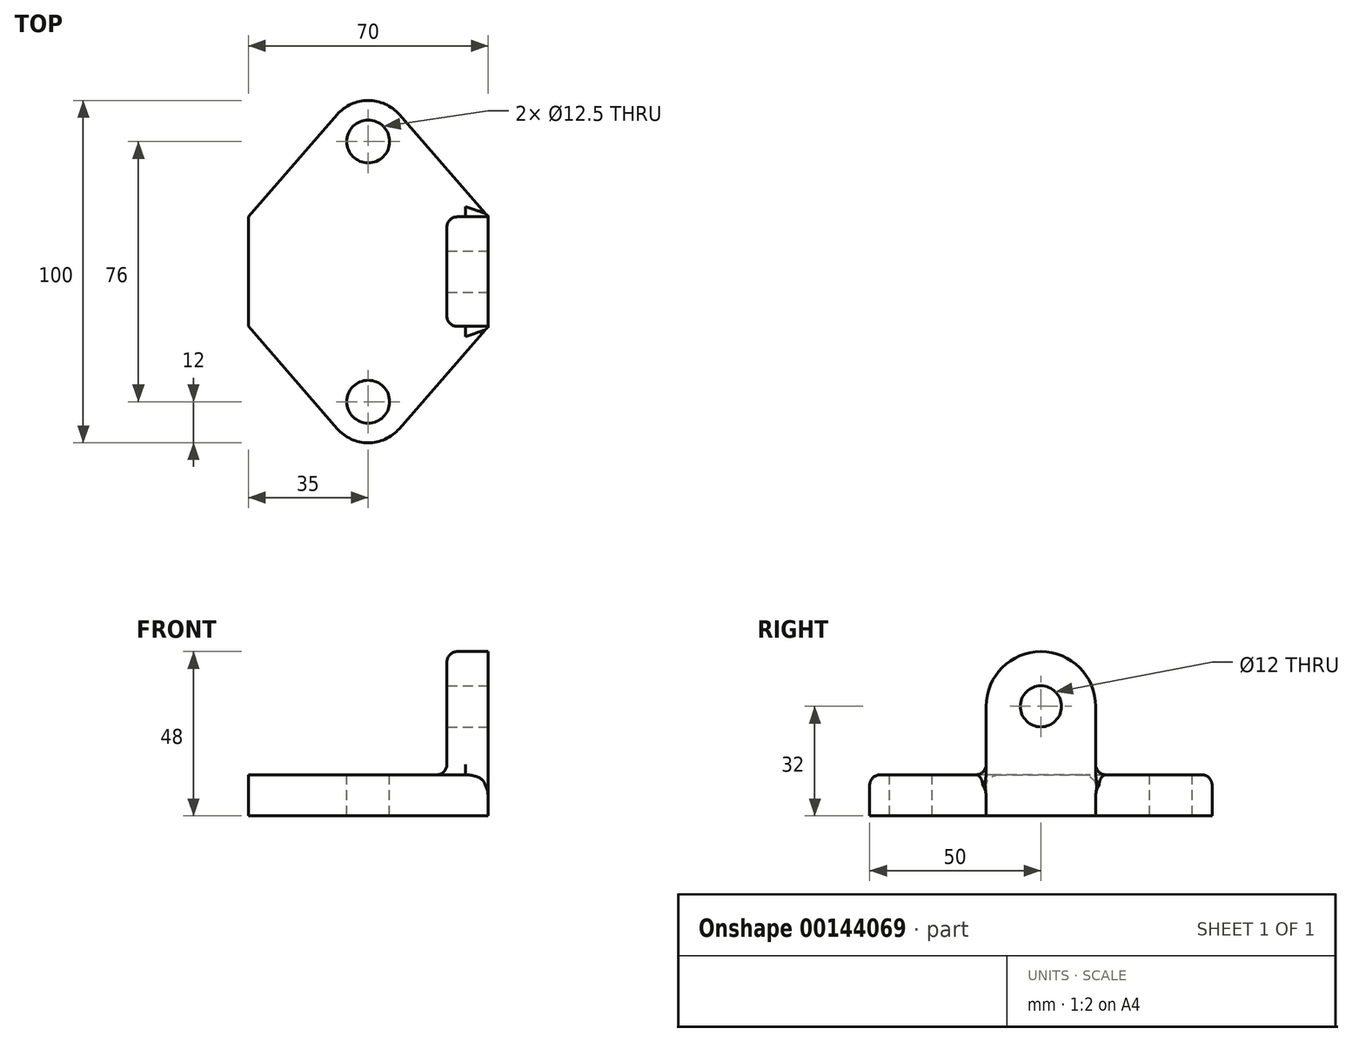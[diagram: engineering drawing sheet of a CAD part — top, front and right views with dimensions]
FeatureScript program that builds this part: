
annotation { "Feature Type Name" : "Feature", "Feature Type Description" : "" }
export const myFeature = defineFeature(function(context is Context, id is Id, definition is map)
    precondition{}
    {
        {
            var Q0;
            Q0=qCreatedBy(makeId("Top.planeOp"),FACE);
            var sketch = newSketch(context, id + "F0", { "sketchPlane" : qUnion([Q0])});
            skLineSegment(sketch, "E0", {"start": v(0, 62.74) * mm, "end": v(0, -56.64) * mm, "construction": true});
            skLineSegment(sketch, "E1.bottom", {"start": v(-35, 0) * mm, "end": v(35, 0) * mm});
            skLineSegment(sketch, "E1.left", {"start": v(-35, 0) * mm, "end": v(-35, -16) * mm});
            skLineSegment(sketch, "E1.right", {"start": v(35, 0) * mm, "end": v(35, -16) * mm});
            skLineSegment(sketch, "E2", {"start": v(-35, -16) * mm, "end": v(-9.06, -45.87) * mm});
            skLineSegment(sketch, "E3", {"start": v(-9.06, -45.87) * mm, "end": v(9.06, -45.87) * mm});
            skLineSegment(sketch, "E4", {"start": v(9.06, -45.87) * mm, "end": v(35, -16) * mm});
            skArc(sketch, "E5", {"start": v(-9.06, -45.87) * mm, "mid": v(0, -50) * mm, "end": v(9.06, -45.87) * mm});
            skCircle(sketch, "E6", {"center": v(0, -38) * mm, "radius": 6.25 * mm});
            skSolve(sketch);
        }
        {
            var Q0;
            Q0=makeQuery(id+"F0.imprint","IMPRINT",FACE,{"disambiguationData":[TD([[makeQuery(id+"F0.imprint","IMPRINT",EDGE,{"derivedFrom":sQuery(id+"F0.wireOp",EDGE,"E1.bottom")}),-1.0]])]});
            var Q1;
            Q1=makeQuery(id+"F0.imprint","IMPRINT",FACE,{"disambiguationData":[TD([[makeQuery(id+"F0.imprint","IMPRINT",EDGE,{"derivedFrom":sQuery(id+"F0.wireOp",EDGE,"E3")}),-1.0]])]});
            var Q2;
            Q2=makeQuery(id+"F0.imprint","IMPRINT",FACE,{"disambiguationData":[TD([[makeQuery(id+"F0.imprint","IMPRINT",EDGE,{"derivedFrom":sQuery(id+"F0.wireOp",EDGE,"E6")}),1.0]])]});
            extrude(context, id + "F1", {"entities" : qUnion([Q0, Q1, Q2]), "depth" : 12 * mm});
        }
        {
            var Q0;
            Q0=makeQuery(id+"F1.opExtrude","SWEPT_BODY",BODY,{"disambiguationData":[OSD([sQuery(id+"F0.wireOp",EDGE,"E1.bottom"),sQuery(id+"F0.wireOp",EDGE,"E1.left"),sQuery(id+"F0.wireOp",EDGE,"E1.right"),sQuery(id+"F0.wireOp",EDGE,"E2"),sQuery(id+"F0.wireOp",EDGE,"E4"),sQuery(id+"F0.wireOp",EDGE,"E5")])]});
            var Q1;
            Q1=qCreatedBy(makeId("Front.planeOp"),FACE);
            mirror(context, id + "F2", {"operationType" : NewBodyOperationType.ADD, "entities" : qUnion([Q0]), "mirrorPlane" : qUnion([Q1])});
        }
        {
            var Q0;
            {var subQ0=makeQuery(id+"F1.opExtrude","SWEPT_FACE",FACE,{"disambiguationData":[OSD([sQuery(id+"F0.wireOp",EDGE,"E1.right")])]});Q0=makeQuery(id+"F2.boolean.opBoolean","MERGE",FACE,{"derivedFrom":[subQ0,makeQuery(id+"F2.opPattern","COPY",FACE,{"derivedFrom":subQ0,"instanceName":"1"})]});}
            var sketch = newSketch(context, id + "F3", { "sketchPlane" : qUnion([Q0])});
            skLineSegment(sketch, "E7.bottom", {"start": v(-16, 0) * mm, "end": v(16, 0) * mm});
            skLineSegment(sketch, "E7.top", {"start": v(-16, 32) * mm, "end": v(16, 32) * mm});
            skLineSegment(sketch, "E7.left", {"start": v(-16, 0) * mm, "end": v(-16, 32) * mm});
            skLineSegment(sketch, "E7.right", {"start": v(16, 0) * mm, "end": v(16, 32) * mm});
            skArc(sketch, "E8", {"start": v(16, 32) * mm, "mid": v(0, 48) * mm, "end": v(-16, 32) * mm});
            skSolve(sketch);
        }
        {
            var Q0;
            Q0=makeQuery(id+"F3.imprint","IMPRINT",FACE,{"disambiguationData":[TD([[makeQuery(id+"F3.imprint","IMPRINT",EDGE,{"derivedFrom":sQuery(id+"F3.wireOp",EDGE,"E7.top")}),1.0]])]});
            var Q1;
            {var subQ0=sQuery(id+"F3.wireOp",EDGE,"E7.top");Q1=makeQuery(id+"F3.imprint","IMPRINT",FACE,{"disambiguationData":[TD([[makeQuery(id+"F3.imprint","IMPRINT",EDGE,{"derivedFrom":subQ0}),-1.0]])]});}
            var Q2;
            {var subQ0=sQuery(id+"F3.wireOp",EDGE,"E7.bottom");Q2=makeQuery(id+"F3.imprint","IMPRINT",FACE,{"disambiguationData":[TD([[makeQuery(id+"F3.imprint","IMPRINT",EDGE,{"derivedFrom":subQ0}),-1.0]])]});}
            extrude(context, id + "F4", {"entities" : qUnion([Q0, Q1, Q2]), "operationType" : NewBodyOperationType.ADD, "oppositeDirection" : true, "depth" : 12 * mm});
        }
        {
            var Q0;
            {var subQ0=makeQuery(id+"F1.opExtrude","CAP_FACE",FACE,{"disambiguationData":[OSD([sQuery(id+"F0.wireOp",EDGE,"E1.bottom"),sQuery(id+"F0.wireOp",EDGE,"E1.left"),sQuery(id+"F0.wireOp",EDGE,"E1.right"),sQuery(id+"F0.wireOp",EDGE,"E2"),sQuery(id+"F0.wireOp",EDGE,"E4"),sQuery(id+"F0.wireOp",EDGE,"E5")])],"isStart":false});Q0=makeQuery(id+"F2.boolean.opBoolean","MERGE",FACE,{"derivedFrom":[subQ0,makeQuery(id+"F2.opPattern","COPY",FACE,{"derivedFrom":subQ0,"instanceName":"1"})]});}
            var sketch = newSketch(context, id + "F5", { "sketchPlane" : qUnion([Q0])});
            skCircle(sketch, "E9.0", {"center": v(0, -38) * mm, "radius": 6.25 * mm});
            skSolve(sketch);
        }
        {
            var Q0;
            Q0=makeQuery(id+"F5.imprint","IMPRINT",FACE,{"disambiguationData":[TD([[makeQuery(id+"F5.imprint","IMPRINT",EDGE,{"derivedFrom":sQuery(id+"F5.wireOp",EDGE,"E9.0")}),-1.0]])]});
            var sketch = newSketch(context, id + "F6", { "sketchPlane" : qUnion([Q0])});
            skCircle(sketch, "E10.0", {"center": v(0, 38) * mm, "radius": 6.25 * mm});
            skSolve(sketch);
        }
        {
            var Q0;
            Q0 = qSketchRegion(id + "F6", true);
            var Q1;
            Q1 = qSketchRegion(id + "F5", true);
            extrude(context, id + "F7", {"entities" : qUnion([Q0, Q1]), "operationType" : NewBodyOperationType.REMOVE, "endBound" : BoundingType.THROUGH_ALL, "oppositeDirection" : true, "depth" : 25 * mm});
        }
        {
            var Q0;
            {var subQ0=makeQuery(id+"F1.opExtrude","SWEPT_FACE",FACE,{"disambiguationData":[OSD([sQuery(id+"F0.wireOp",EDGE,"E1.right")])]});Q0=makeQuery(id+"F4.boolean.opBoolean","MERGE",FACE,{"derivedFrom":[makeQuery(id+"F2.boolean.opBoolean","MERGE",FACE,{"derivedFrom":[subQ0,makeQuery(id+"F2.opPattern","COPY",FACE,{"derivedFrom":subQ0,"instanceName":"1"})]}),makeQuery(id+"F4.opExtrude","CAP_FACE",FACE,{"disambiguationData":[OSD([sQuery(id+"F3.wireOp",EDGE,"E7.bottom"),sQuery(id+"F3.wireOp",EDGE,"E7.left"),sQuery(id+"F3.wireOp",EDGE,"E7.right"),sQuery(id+"F3.wireOp",EDGE,"E8")])],"isStart":true})]});}
            var sketch = newSketch(context, id + "F8", { "sketchPlane" : qUnion([Q0])});
            skCircle(sketch, "E11", {"center": v(0, 32) * mm, "radius": 6 * mm});
            skSolve(sketch);
        }
        {
            var Q0;
            Q0 = qSketchRegion(id + "F8", true);
            extrude(context, id + "F9", {"entities" : qUnion([Q0]), "operationType" : NewBodyOperationType.REMOVE, "endBound" : BoundingType.THROUGH_ALL, "oppositeDirection" : true, "depth" : 25 * mm});
        }
        {
            var Q0;
            Q0=makeQuery(id+"F2.opPattern","COPY",EDGE,{"derivedFrom":makeQuery(id+"F1.opExtrude","CAP_EDGE",EDGE,{"disambiguationData":[OSD([sQuery(id+"F0.wireOp",EDGE,"E2")])],"isStart":false}),"instanceName":"1"});
            var Q1;
            Q1=makeQuery(id+"F1.opExtrude","CAP_EDGE",EDGE,{"disambiguationData":[OSD([sQuery(id+"F0.wireOp",EDGE,"E4")])],"isStart":false});
            var Q2;
            Q2=makeQuery(id+"FWKPYHZQDnc0K3y_1.1.F2.opPattern","COPY",EDGE,{"derivedFrom":makeQuery(id+"F4.opExtrude","CAP_EDGE",EDGE,{"disambiguationData":[OSD([sQuery(id+"F3.wireOp",EDGE,"E8")])],"isStart":false}),"instanceName":"1"});
            var Q3;
            Q3=makeQuery(id+"F4.opExtrude","CAP_EDGE",EDGE,{"disambiguationData":[OSD([sQuery(id+"F3.wireOp",EDGE,"E8")])],"isStart":false});
            fillet(context, id + "F10", {"entities" : qUnion([Q0, Q1, Q2, Q3]), "radius" : 3 * mm, "tangentPropagation" : true, "allowEdgeOverflow" : false});
        }
        {
            var Q0;
            {var subQ0=makeQuery(id+"F1.opExtrude","CAP_FACE",FACE,{"disambiguationData":[OSD([sQuery(id+"F0.wireOp",EDGE,"E1.bottom"),sQuery(id+"F0.wireOp",EDGE,"E1.left"),sQuery(id+"F0.wireOp",EDGE,"E1.right"),sQuery(id+"F0.wireOp",EDGE,"E2"),sQuery(id+"F0.wireOp",EDGE,"E4"),sQuery(id+"F0.wireOp",EDGE,"E5")])],"isStart":false});Q0=makeQuery(id+"FWKPYHZQDnc0K3y_1.1.F2.opPattern","COPY",EDGE,{"derivedFrom":makeQuery(id+"F4.boolean.opBoolean","INTERSECT",EDGE,{"derivedFrom":[makeQuery(id+"F2.boolean.opBoolean","MERGE",FACE,{"derivedFrom":[subQ0,makeQuery(id+"F2.opPattern","COPY",FACE,{"derivedFrom":subQ0,"instanceName":"1"})]}),makeQuery(id+"F4.opExtrude","CAP_FACE",FACE,{"disambiguationData":[OSD([sQuery(id+"F3.wireOp",EDGE,"E7.bottom"),sQuery(id+"F3.wireOp",EDGE,"E7.left"),sQuery(id+"F3.wireOp",EDGE,"E7.right"),sQuery(id+"F3.wireOp",EDGE,"E8")])],"isStart":false})]}),"instanceName":"1"});}
            var Q1;
            {var subQ0=makeQuery(id+"F1.opExtrude","CAP_FACE",FACE,{"disambiguationData":[OSD([sQuery(id+"F0.wireOp",EDGE,"E1.bottom"),sQuery(id+"F0.wireOp",EDGE,"E1.left"),sQuery(id+"F0.wireOp",EDGE,"E1.right"),sQuery(id+"F0.wireOp",EDGE,"E2"),sQuery(id+"F0.wireOp",EDGE,"E4"),sQuery(id+"F0.wireOp",EDGE,"E5")])],"isStart":false});Q1=makeQuery(id+"F4.boolean.opBoolean","INTERSECT",EDGE,{"derivedFrom":[makeQuery(id+"F2.boolean.opBoolean","MERGE",FACE,{"derivedFrom":[subQ0,makeQuery(id+"F2.opPattern","COPY",FACE,{"derivedFrom":subQ0,"instanceName":"1"})]}),makeQuery(id+"F4.opExtrude","SWEPT_FACE",FACE,{"disambiguationData":[OSD([sQuery(id+"F3.wireOp",EDGE,"E7.left")])]})]});}
            fillet(context, id + "F11", {"entities" : qUnion([Q0, Q1]), "radius" : 3 * mm, "tangentPropagation" : true, "allowEdgeOverflow" : false});
        }
    });
